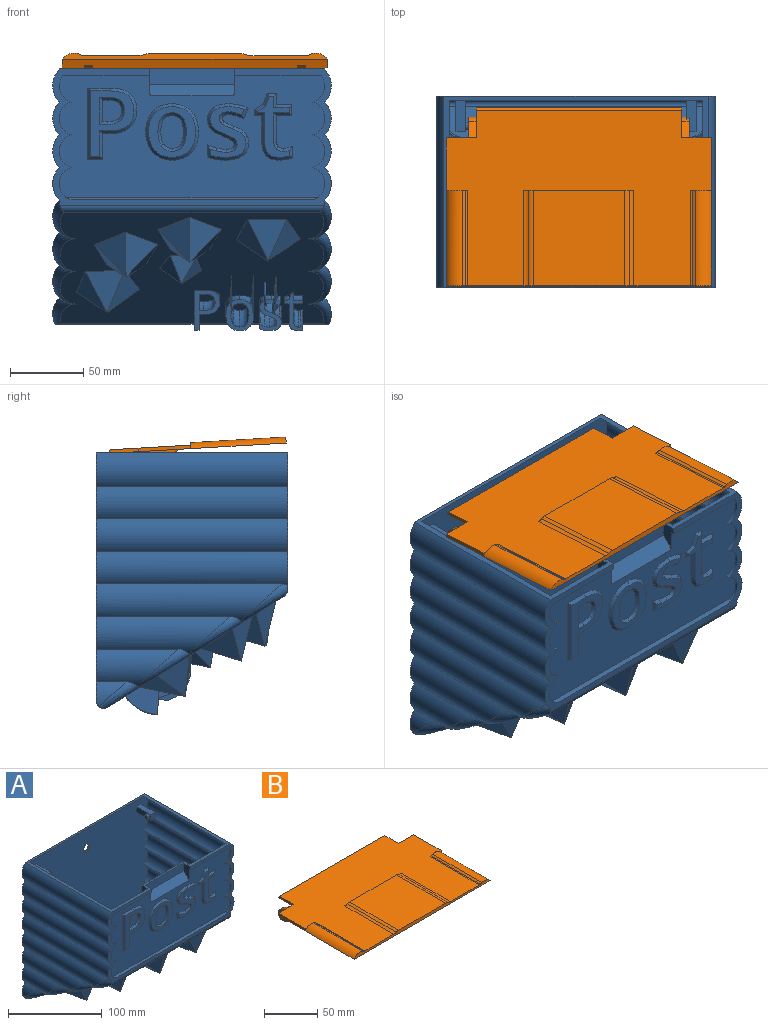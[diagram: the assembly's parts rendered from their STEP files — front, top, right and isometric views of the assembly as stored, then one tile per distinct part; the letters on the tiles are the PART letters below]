
ASSEMBLY  parts=2 mates=1
PART A: 296 faces, bbox 194.2x139.1x180.6 mm
  f0: cylinder r=13.63mm len=124mm, axis (0,1,0), area 3216.3mm2, adj f1,f8,f50,f294
  f1: cylinder r=13.63mm len=124mm, axis (0,1,0), area 3216.3mm2, adj f0,f2,f8,f294
  f2: cylinder r=13.63mm len=124mm, axis (0,1,0), area 3216.3mm2, adj f1,f3,f8,f294
  f3: cylinder r=13.63mm len=124mm, axis (0,1,0), area 3297.8mm2, adj f2,f8,f24,f294
  f4: cylinder r=13.63mm len=124mm, axis (0,1,0), area 3297.8mm2, adj f5,f8,f24,f294
  f5: cylinder r=13.63mm len=124mm, axis (0,1,0), area 3216.3mm2, adj f4,f6,f8,f294
  f6: cylinder r=13.63mm len=124mm, axis (0,1,0), area 3216.3mm2, adj f5,f7,f8,f294
  f7: cylinder r=13.63mm len=124mm, axis (0,1,0), area 3216.3mm2, adj f6,f8,f51,f294
  f8: plane 184.57x168.8mm, normal (0,-1,0), area 30406.4mm2, adj f0,f1,f2,f3,f4,f5,f6,f7
  f9: plane 182.54x84.64mm, normal (0,-1,0), area 10256.5mm2, adj f10,f11,f31,f32,f70,f71,f72,f73
  f10: cylinder r=5mm len=3mm, axis (0,-1,0), area 4.8mm2, adj f9,f31,f164
  f11: cylinder r=5mm len=3mm, axis (0,-1,0), area 4.8mm2, adj f9,f32,f164
  f12: plane 189.57x168.8mm, normal (0,1,0), area 31462.7mm2, adj f14,f15,f16,f17,f18,f19,f20,f21
  f13: plane 189.86x93.45mm, normal (0,-1,0), area 2168.8mm2, adj f20,f21,f22,f23,f24,f25,f26,f27
  f14: cylinder r=16.13mm len=55.43mm, axis (0,1,0), area 1109.7mm2, adj f12,f15,f30,f39,f41
  f15: cylinder r=16.13mm len=20.21mm, axis (0,1,0), area 195.6mm2, adj f12,f14,f41,f43
  f16: cylinder r=16.13mm len=20.21mm, axis (0,1,0), area 195.6mm2, adj f12,f17,f43,f44
  f17: cylinder r=16.13mm len=55.43mm, axis (0,1,0), area 1109.7mm2, adj f12,f16,f18,f42,f44
  f18: cylinder r=16.13mm len=90.65mm, axis (0,1,0), area 1971.9mm2, adj f12,f17,f19,f40,f42
  f19: cylinder r=16.13mm len=125.87mm, axis (0,1,0), area 2834.1mm2, adj f12,f18,f20,f38,f40
  f20: cylinder r=16.13mm len=130mm, axis (0,1,0), area 3184.8mm2, adj f12,f13,f19,f21,f38
  f21: cylinder r=16.13mm len=130mm, axis (0,1,0), area 3182.6mm2, adj f12,f13,f20,f22
  f22: cylinder r=16.13mm len=130mm, axis (0,1,0), area 3182.6mm2, adj f12,f13,f21,f23
  f23: cylinder r=16.13mm len=130mm, axis (0,1,0), area 3249.7mm2, adj f12,f13,f22,f24
  f24: plane 180x130mm, normal (0,0,1), area 2052.6mm2, adj f3,f4,f8,f12,f13,f23,f25,f31
  f25: cylinder r=16.13mm len=130mm, axis (0,1,0), area 3249.7mm2, adj f12,f13,f24,f26
  f26: cylinder r=16.13mm len=130mm, axis (0,1,0), area 3182.6mm2, adj f12,f13,f25,f27
  f27: cylinder r=16.13mm len=130mm, axis (0,1,0), area 3182.6mm2, adj f12,f13,f26,f28
  f28: cylinder r=16.13mm len=130mm, axis (0,1,0), area 3184.8mm2, adj f12,f13,f27,f29,f35
  f29: cylinder r=16.13mm len=125.87mm, axis (0,1,0), area 2834.1mm2, adj f12,f28,f30,f35,f37
  f30: cylinder r=16.13mm len=90.65mm, axis (0,1,0), area 1971.9mm2, adj f12,f14,f29,f37,f39
  f31: plane 15.29x10mm, normal (1,0,0), area 118.8mm2, adj f9,f10,f13,f24,f33,f72,f164
  f32: plane 15.29x10mm, normal (-1,0,0), area 118.8mm2, adj f9,f11,f13,f24,f33,f70,f164
  f33: plane 58.15x10.29mm, normal (0,-1,0), area 598.2mm2, adj f24,f31,f32,f164
  f34: plane 181.94x122.37mm, normal (0,-0.53,-0.85), area 18554mm2, adj f35,f36,f37,f38,f39,f40,f41,f42
  f35: bspline ~40.65x29.36mm, area 302mm2, adj f13,f28,f29,f34,f36,f37
  f36: cylinder r=5mm len=179.61mm, axis (-1,0,0), area 892.5mm2, adj f13,f34,f35,f38
  f37: bspline ~52.64x32.27mm, area 346mm2, adj f29,f30,f34,f35,f39
  f38: bspline ~40.65x29.36mm, area 302mm2, adj f13,f19,f20,f34,f36,f40
  f39: bspline ~52.64x32.27mm, area 346mm2, adj f14,f30,f34,f37,f41
  f40: bspline ~52.64x32.27mm, area 346mm2, adj f18,f19,f34,f38,f42
  f41: bspline ~42.45x25.53mm, area 255.1mm2, adj f14,f15,f34,f39,f43
  f42: bspline ~52.64x32.27mm, area 346mm2, adj f17,f18,f34,f40,f44
  f43: cylinder r=5mm len=189.34mm, axis (1,0,0), area 1977.5mm2, adj f12,f15,f16,f34,f41,f44
  f44: bspline ~42.45x25.53mm, area 255.1mm2, adj f16,f17,f34,f42,f43
  f45: cylinder r=13.63mm len=55.16mm, axis (0,1,0), area 1092.7mm2, adj f8,f46,f52,f64,f66
  f46: cylinder r=13.63mm len=19.94mm, axis (0,1,0), area 184.2mm2, adj f8,f45,f66,f68
  f47: cylinder r=13.63mm len=19.94mm, axis (0,1,0), area 184.2mm2, adj f8,f48,f68,f69
  f48: cylinder r=13.63mm len=55.16mm, axis (0,1,0), area 1092.7mm2, adj f8,f47,f49,f67,f69
  f49: cylinder r=13.63mm len=90.38mm, axis (0,1,0), area 2006.2mm2, adj f8,f48,f50,f65,f67
  f50: cylinder r=13.63mm len=125mm, axis (0,1,0), area 2891.2mm2, adj f0,f8,f49,f63,f65,f291,f294
  f51: cylinder r=13.63mm len=125mm, axis (0,1,0), area 2891.2mm2, adj f7,f8,f52,f60,f62,f293,f294
  f52: cylinder r=13.63mm len=90.38mm, axis (0,1,0), area 2006.2mm2, adj f8,f45,f51,f62,f64
  f53: plane 15.29x9mm, normal (-1,0,0), area 137.6mm2, adj f24,f54,f58,f294
  f54: cylinder r=7.5mm len=9mm, axis (0,-1,0), area 106mm2, adj f53,f55,f58,f294
  f55: plane 48.15x9mm, normal (0,0,-1), area 433.4mm2, adj f54,f56,f58,f294
  f56: cylinder r=7.5mm len=9mm, axis (0,-1,0), area 106mm2, adj f55,f57,f58,f294
  f57: plane 15.29x9mm, normal (1,0,0), area 137.6mm2, adj f24,f56,f58,f294
  f58: plane 63.15x22.79mm, normal (0,1,0), area 1414.9mm2, adj f24,f53,f54,f55,f56,f57
  f59: plane 179.57x120mm, normal (0,0.53,0.85), area 24859.7mm2, adj f60,f61,f62,f63,f64,f65,f66,f67
  f60: bspline ~36.4x24.81mm, area 142mm2, adj f51,f59,f61,f62,f293
  f61: cylinder r=2.5mm len=177.1mm, axis (-1,0,0), area 443.1mm2, adj f59,f60,f63,f292
  f62: bspline ~43.98x27.27mm, area 177.8mm2, adj f51,f52,f59,f60,f64
  f63: bspline ~36.4x24.81mm, area 142mm2, adj f50,f59,f61,f65,f291
  f64: bspline ~43.98x27.27mm, area 177.8mm2, adj f45,f52,f59,f62,f66
  f65: bspline ~43.98x27.27mm, area 177.8mm2, adj f49,f50,f59,f63,f67
  f66: bspline ~33.79x20.69mm, area 129.8mm2, adj f45,f46,f59,f64,f68
  f67: bspline ~43.98x27.27mm, area 177.8mm2, adj f48,f49,f59,f65,f69
  f68: cylinder r=2.5mm len=184.3mm, axis (1,0,0), area 972.4mm2, adj f8,f46,f47,f59,f66,f69
  f69: bspline ~33.79x20.69mm, area 129.8mm2, adj f47,f48,f59,f67,f68
  f70: plane 58.89x2mm, normal (0,0,-1), area 117.8mm2, adj f9,f13,f32,f71
  f71: cylinder r=11.63mm len=18.07mm, axis (0,-1,0), area 44.4mm2, adj f9,f13,f70,f79
  f72: plane 58.89x2mm, normal (0,0,-1), area 117.8mm2, adj f9,f13,f31,f73
  f73: cylinder r=11.63mm len=18.07mm, axis (0,-1,0), area 44.4mm2, adj f9,f13,f72,f74
  f74: cylinder r=11.63mm len=22.2mm, axis (0,-1,0), area 58.9mm2, adj f9,f13,f73,f75
  f75: cylinder r=11.63mm len=22.2mm, axis (0,-1,0), area 58.9mm2, adj f9,f13,f74,f76
  f76: cylinder r=11.63mm len=22.2mm, axis (0,-1,0), area 54.7mm2, adj f9,f13,f75,f295
  f77: cylinder r=11.63mm len=22.2mm, axis (0,-1,0), area 54.7mm2, adj f9,f13,f78,f295
  f78: cylinder r=11.63mm len=22.2mm, axis (0,-1,0), area 58.9mm2, adj f9,f13,f77,f79
  f79: cylinder r=11.63mm len=22.2mm, axis (0,-1,0), area 58.9mm2, adj f9,f13,f71,f78
  f80: plane 45.89x30.91mm, normal (0,-1,0), area 560mm2, adj f104,f105,f106,f107,f108,f109,f110,f111
  f81: plane 14.86x13.3mm, normal (0,-1,0), area 163.4mm2, adj f113,f114,f115,f116,f117,f118,f119
  f82: plane 35.57x33.08mm, normal (0,-1,0), area 479mm2, adj f86,f87,f88,f89,f90,f91,f92,f93
  f83: plane 22.89x16.03mm, normal (0,-1,0), area 284.3mm2, adj f96,f97,f98,f99,f100,f101,f102,f103
  f84: plane 35.86x25.56mm, normal (0,-1,0), area 354mm2, adj f138,f139,f140,f141,f142,f143,f144,f145
  f85: plane 42.68x22.79mm, normal (0,-1,0), area 326.1mm2, adj f120,f121,f122,f123,f124,f125,f126,f127
  f86: bspline ~13.32x6.41mm, area 39.2mm2, adj f9,f82,f87,f88
  f87: bspline ~9.41x4.07mm, area 26.3mm2, adj f9,f82,f86,f89
  f88: bspline ~14.11x6.19mm, area 41mm2, adj f9,f82,f86,f90
  f89: bspline ~7.56x7.25mm, area 24.6mm2, adj f9,f82,f87,f91
  f90: bspline ~10.2x3.98mm, area 28.5mm2, adj f9,f82,f88,f92
  f91: bspline ~10.17x3.97mm, area 28.4mm2, adj f9,f82,f89,f93
  f92: bspline ~7.6x7.25mm, area 24.7mm2, adj f9,f82,f90,f94
  f93: bspline ~14.15x6.23mm, area 41.1mm2, adj f9,f82,f91,f95
  f94: bspline ~9.41x4.09mm, area 26.3mm2, adj f9,f82,f92,f95
  f95: bspline ~13.28x6.47mm, area 39.1mm2, adj f9,f82,f93,f94
  f96: bspline ~9.34x3.79mm, area 25.8mm2, adj f82,f83,f97,f98
  f97: bspline ~7.55x4.75mm, area 22mm2, adj f82,f83,f96,f99
  f98: bspline ~9.4x3.77mm, area 26mm2, adj f82,f83,f96,f100
  f99: bspline ~7.5x4.74mm, area 21.8mm2, adj f82,f83,f97,f101
  f100: bspline ~7.51x4.8mm, area 22mm2, adj f82,f83,f98,f102
  f101: bspline ~9.36x3.79mm, area 25.9mm2, adj f82,f83,f99,f103
  f102: bspline ~7.56x4.82mm, area 22.1mm2, adj f82,f83,f100,f103
  f103: bspline ~9.4x3.81mm, area 26mm2, adj f82,f83,f101,f102
  f104: plane 10.27x2mm, normal (0,-0.71,-0.71), area 23.4mm2, adj f9,f80,f105,f106
  f105: plane 19.23x2mm, normal (0.71,-0.71,0), area 48.7mm2, adj f9,f80,f104,f107
  f106: plane 48.43x2mm, normal (-0.71,-0.71,0), area 131.3mm2, adj f9,f80,f104,f108
  f107: plane 6.4x2mm, normal (0,-0.71,-0.71), area 15.3mm2, adj f9,f80,f105,f109
  f108: plane 15.47x2mm, normal (0,-0.71,0.71), area 40.9mm2, adj f9,f80,f106,f110
  f109: bspline ~13.9x5.67mm, area 39.9mm2, adj f9,f80,f107,f111
  f110: bspline ~13.4x5.34mm, area 38.2mm2, adj f9,f80,f108,f112
  f111: bspline ~11.96x6.18mm, area 35.3mm2, adj f9,f80,f109,f112
  f112: bspline ~11.31x5.86mm, area 33.2mm2, adj f9,f80,f110,f111
  f113: bspline ~6.84x4mm, area 19mm2, adj f80,f81,f114,f115
  f114: bspline ~7.01x4.4mm, area 19.9mm2, adj f80,f81,f113,f116
  f115: bspline ~7.5x3.72mm, area 20.6mm2, adj f80,f81,f113,f117
  f116: bspline ~8.33x3.87mm, area 23mm2, adj f80,f81,f114,f118
  f117: plane 6.66x2mm, normal (0,-0.71,-0.71), area 16mm2, adj f80,f81,f115,f119
  f118: plane 5.38x2mm, normal (0,-0.71,0.71), area 12.4mm2, adj f80,f81,f116,f119
  f119: plane 18.37x2mm, normal (0.71,-0.71,0), area 46.3mm2, adj f80,f81,f117,f118
  f120: plane 7.2x4.51mm, normal (-0.37,-0.71,0.6), area 17.8mm2, adj f9,f85,f121,f122
  f121: plane 9.17x4.3mm, normal (-0.66,-0.71,0.25), area 22.6mm2, adj f9,f85,f120,f123
  f122: plane 4.27x2mm, normal (-0.71,-0.71,0), area 7.7mm2, adj f9,f85,f120,f124
  f123: plane 6.46x2mm, normal (0,-0.71,0.71), area 13.5mm2, adj f9,f85,f121,f125
  f124: plane 6.83x2mm, normal (0,-0.71,-0.71), area 13.7mm2, adj f9,f85,f122,f126
  f125: plane 9.89x2mm, normal (0.71,-0.71,0), area 22.3mm2, adj f9,f85,f123,f127
  f126: plane 19.85x2mm, normal (-0.71,-0.71,0), area 53.3mm2, adj f9,f85,f124,f128
  f127: plane 12.37x2mm, normal (0,-0.71,0.71), area 29.3mm2, adj f9,f85,f125,f129
  f128: bspline ~9.2x4.25mm, area 25.7mm2, adj f9,f85,f126,f130
  f129: plane 7.59x2mm, normal (0.71,-0.71,0), area 15.8mm2, adj f9,f85,f127,f131
  f130: bspline ~8.83x4.41mm, area 24.9mm2, adj f9,f85,f128,f132
  f131: plane 12.37x2mm, normal (0,-0.71,-0.71), area 29.3mm2, adj f9,f85,f129,f133
  f132: bspline ~9.28x3.52mm, area 23.8mm2, adj f9,f85,f130,f134
  f133: plane 19.85x2mm, normal (0.71,-0.71,0), area 53.3mm2, adj f9,f85,f131,f135
  f134: plane 7.65x2.14mm, normal (0.71,-0.71,0), area 15.6mm2, adj f9,f85,f132,f136
  f135: bspline ~4.7x3.24mm, area 12.4mm2, adj f9,f85,f133,f137
  f136: bspline ~6.94x3.16mm, area 15.5mm2, adj f9,f85,f134,f137
  f137: bspline ~4.5x3.04mm, area 11.7mm2, adj f9,f85,f135,f136
  f138: bspline ~4.33x4.13mm, area 11.6mm2, adj f9,f84,f139,f140
  f139: bspline ~4.84x2.72mm, area 12.8mm2, adj f9,f84,f138,f141
  f140: bspline ~7.05x4.91mm, area 19.4mm2, adj f9,f84,f138,f142
  f141: bspline ~7.64x4.98mm, area 22.5mm2, adj f9,f84,f139,f143
  f142: bspline ~5.7x4.04mm, area 15.1mm2, adj f9,f84,f140,f144
  f143: bspline ~10.85x4.33mm, area 30.4mm2, adj f9,f84,f141,f145
  f144: bspline ~3.95x3.46mm, area 9.5mm2, adj f9,f84,f142,f146
  f145: bspline ~13.02x4.73mm, area 34mm2, adj f9,f84,f143,f147
  f146: bspline ~3.34x2.74mm, area 8.2mm2, adj f9,f84,f144,f148
  f147: plane 7.43x4.27mm, normal (0.65,-0.71,-0.27), area 16.7mm2, adj f9,f84,f145,f149
  f148: bspline ~7.51x5.18mm, area 24.6mm2, adj f9,f84,f146,f150
  f149: bspline ~5.98x3.86mm, area 13.2mm2, adj f9,f84,f147,f151
  f150: bspline ~6.7x2.9mm, area 18.5mm2, adj f9,f84,f148,f152
  f151: bspline ~5.54x2.77mm, area 15.1mm2, adj f9,f84,f149,f153
  f152: bspline ~7.18x4.16mm, area 15.3mm2, adj f9,f84,f150,f154
  f153: bspline ~6.48x4.42mm, area 20.5mm2, adj f9,f84,f151,f155
  f154: plane 8.45x2.1mm, normal (-0.71,-0.71,0), area 17.4mm2, adj f9,f84,f152,f156
  f155: bspline ~4x3.47mm, area 10.9mm2, adj f9,f84,f153,f157
  f156: bspline ~5.95x3.55mm, area 13.3mm2, adj f9,f84,f154,f158
  f157: bspline ~7.81x4.96mm, area 20.4mm2, adj f9,f84,f155,f159
  f158: bspline ~6.89x2.52mm, area 19mm2, adj f9,f84,f156,f160
  f159: bspline ~7.42x5mm, area 19.5mm2, adj f9,f84,f157,f161
  f160: bspline ~11.85x4.58mm, area 33.3mm2, adj f9,f84,f158,f162
  f161: bspline ~4.38x4.19mm, area 11.8mm2, adj f9,f84,f159,f163
  f162: bspline ~8.69x5.16mm, area 25.5mm2, adj f9,f84,f160,f163
  f163: bspline ~4.73x2.76mm, area 12.5mm2, adj f9,f84,f161,f162
  f164: plane 58.32x8.17mm, normal (0,-0.71,0.71), area 655.2mm2, adj f9,f10,f11,f31,f32,f33
  f165: plane 4.05x2.5mm, normal (0.87,0,-0.49), area 11.6mm2, adj f8,f12,f166,f170
  f166: plane 4.05x2.5mm, normal (0.87,0,0.49), area 11.6mm2, adj f8,f12,f165,f167
  f167: cylinder r=3mm len=5.23mm, axis (0,-1,0), area 15.9mm2, adj f8,f12,f166,f168
  f168: plane 4.05x2.5mm, normal (-0.87,0,0.49), area 11.6mm2, adj f8,f12,f167,f169
  f169: plane 4.05x2.5mm, normal (-0.87,0,-0.49), area 11.6mm2, adj f8,f12,f168,f170
  f170: cylinder r=3mm len=5.23mm, axis (0,-1,0), area 15.9mm2, adj f8,f12,f165,f169
  f171: plane 7.63x6.7mm, normal (0,-1,0), area 51.2mm2, adj f172,f173,f174,f175
  f172: plane 21.7x6.7mm, normal (0,0,-1), area 145.4mm2, adj f8,f171,f174,f175
  f173: plane 21.7x6.7mm, normal (0,0,1), area 145.4mm2, adj f8,f171,f174,f175
  f174: plane 21.7x7.63mm, normal (-1,0,0), area 165.7mm2, adj f8,f171,f172,f173
  f175: plane 21.7x7.63mm, normal (1,0,0), area 141.1mm2, adj f8,f171,f172,f173,f176
  f176: cone r=2.8mm half-angle=10deg, axis (-1,0,0), area 48.5mm2, adj f175,f177
  f177: plane 4.54x4.54mm, normal (1,0,0), area 16.2mm2, adj f176
  f178: plane 7.63x6.7mm, normal (0,-1,0), area 51.2mm2, adj f179,f180,f181,f182
  f179: plane 21.7x6.7mm, normal (0,0,-1), area 145.4mm2, adj f8,f178,f181,f182
  f180: plane 21.7x6.7mm, normal (0,0,1), area 145.4mm2, adj f8,f178,f181,f182
  f181: plane 21.7x7.63mm, normal (1,0,0), area 165.7mm2, adj f8,f178,f179,f180
  f182: plane 21.7x7.63mm, normal (-1,0,0), area 141.1mm2, adj f8,f178,f179,f180,f183
  f183: cone r=2.8mm half-angle=10deg, axis (1,0,0), area 48.5mm2, adj f182,f184
  f184: plane 4.54x4.54mm, normal (-1,0,0), area 16.2mm2, adj f183
  f185: plane 30.63x21.68mm, normal (-0.46,-0.86,-0.22), area 381.5mm2, adj f34,f186,f189
  f186: plane 27.35x22.13mm, normal (-0.73,-0.14,-0.67), area 381.5mm2, adj f34,f185,f187
  f187: plane 27.35x26.69mm, normal (0.01,0.31,-0.95), area 381.5mm2, adj f34,f186,f188
  f188: plane 27.08x22.4mm, normal (0.73,-0.15,-0.67), area 381.5mm2, adj f34,f187,f189
  f189: plane 30.63x21.78mm, normal (0.44,-0.87,-0.21), area 381.5mm2, adj f34,f185,f188
  f190: plane 30.63x21.68mm, normal (-0.46,-0.86,-0.22), area 381.5mm2, adj f34,f191,f194
  f191: plane 27.35x22.13mm, normal (-0.73,-0.14,-0.67), area 381.5mm2, adj f34,f190,f192
  f192: plane 27.35x26.69mm, normal (0.01,0.31,-0.95), area 381.5mm2, adj f34,f191,f193
  f193: plane 27.08x22.4mm, normal (0.73,-0.15,-0.67), area 381.5mm2, adj f34,f192,f194
  f194: plane 30.63x21.78mm, normal (0.44,-0.87,-0.21), area 381.5mm2, adj f34,f190,f193
  f195: plane 27.7x21.97mm, normal (-0.75,-0.49,-0.45), area 381.5mm2, adj f34,f196,f199
  f196: plane 30.82x22.8mm, normal (-0.4,0.21,-0.89), area 381.5mm2, adj f34,f195,f197
  f197: plane 30.82x22.1mm, normal (0.5,0.15,-0.85), area 381.5mm2, adj f34,f196,f198
  f198: plane 28.86x22.1mm, normal (0.71,-0.59,-0.39), area 381.5mm2, adj f34,f197,f199
  f199: plane 28.86x26.61mm, normal (-0.06,-0.99,-0.14), area 381.5mm2, adj f34,f195,f198
  f200: plane 19.23x14.72mm, normal (-0.7,-0.61,-0.38), area 167.8mm2, adj f34,f201,f204
  f201: plane 20.42x14.72mm, normal (-0.51,0.14,-0.85), area 167.8mm2, adj f34,f200,f202
  f202: plane 20.42x15.31mm, normal (0.38,0.22,-0.9), area 167.8mm2, adj f34,f201,f203
  f203: plane 18.26x14.64mm, normal (0.75,-0.48,-0.46), area 167.8mm2, adj f34,f202,f204
  f204: plane 19.23x17.61mm, normal (0.08,-0.99,-0.14), area 167.8mm2, adj f34,f200,f203
  f205: plane 28.52x26.68mm, normal (-0.02,-0.99,-0.14), area 381.5mm2, adj f34,f206,f209
  f206: plane 28.1x21.67mm, normal (-0.74,-0.52,-0.43), area 381.5mm2, adj f34,f205,f207
  f207: plane 30.88x22.05mm, normal (-0.43,0.19,-0.88), area 381.5mm2, adj f34,f206,f208
  f208: plane 30.88x21.79mm, normal (0.47,0.17,-0.87), area 381.5mm2, adj f34,f207,f209
  f209: plane 28.52x21.79mm, normal (0.72,-0.56,-0.41), area 381.5mm2, adj f34,f205,f208
  f210: plane 12.14x11.56mm, normal (1,0,0), area 86.4mm2, adj f211,f223,f224,f225
  f211: cylinder r=3mm len=3.57mm, axis (1,0,0), area 8.5mm2, adj f210,f212,f224,f225
  f212: revolved ~5.56x3.23mm, area 16.1mm2, adj f211,f213,f224,f225
  f213: revolved ~6.61x5.86mm, area 25.1mm2, adj f212,f214,f224,f225
  f214: revolved ~10.14x8.03mm, area 48.9mm2, adj f213,f215,f224,f225
  f215: revolved ~11.09x6.95mm, area 81.2mm2, adj f214,f223,f224,f225
  f216: plane 27.06x23.13mm, normal (-1,0,0), area 354.6mm2, adj f34,f217,f224
  f217: cylinder r=27.69mm len=21.82mm, axis (1,0,0), area 83.3mm2, adj f34,f216,f218,f224
  f218: plane 22.34x18.24mm, normal (1,0,0), area 225.8mm2, adj f34,f217,f219,f224
  f219: cylinder r=16.89mm len=13.21mm, axis (1,0,0), area 50.8mm2, adj f34,f218,f220,f224
  f220: revolved ~13.31x8.71mm, area 129.6mm2, adj f34,f219,f221,f224
  f221: revolved ~11.73x10.01mm, area 77.7mm2, adj f34,f220,f222,f224
  f222: revolved ~7.88x6.66mm, area 24.3mm2, adj f34,f221,f224
  f223: cylinder r=14.15mm len=11.02mm, axis (1,0,0), area 37.7mm2, adj f210,f215,f224,f225
  f224: plane 27.43x17.41mm, normal (0,-1,-0.05), area 182.3mm2, adj f34,f210,f211,f212,f213,f214,f215,f216
  f225: plane 11.88x10.43mm, normal (0,-0.53,-0.85), area 108.5mm2, adj f210,f211,f212,f213,f214,f215,f223
  f226: revolved ~13.97x12.01mm, area 102.8mm2, adj f34,f227,f242,f243
  f227: revolved ~7.53x6.86mm, area 52.9mm2, adj f34,f226,f228,f243
  f228: revolved ~7.47x6.99mm, area 53.3mm2, adj f34,f227,f229,f243
  f229: revolved ~13.97x12.05mm, area 103.2mm2, adj f34,f228,f230,f243
  f230: revolved ~18.4x13.45mm, area 110.7mm2, adj f34,f229,f231,f243
  f231: revolved ~21.27x14.09mm, area 119mm2, adj f34,f230,f232,f243
  f232: revolved ~22.19x13.37mm, area 133.8mm2, adj f34,f231,f233,f243
  f233: revolved ~22.26x14.21mm, area 199.4mm2, adj f34,f232,f242,f243
  f234: revolved ~13.88x11.02mm, area 83.3mm2, adj f235,f241,f243,f244
  f235: revolved ~8.91x6.04mm, area 47.8mm2, adj f234,f236,f243,f244
  f236: revolved ~8.94x6.07mm, area 48.6mm2, adj f235,f237,f243,f244
  f237: revolved ~13.88x11mm, area 83.1mm2, adj f236,f238,f243,f244
  f238: revolved ~18.69x13.8mm, area 121.4mm2, adj f237,f239,f243,f244
  f239: revolved ~20.14x12.57mm, area 123.1mm2, adj f238,f240,f243,f244
  f240: revolved ~20.14x12.58mm, area 122.9mm2, adj f239,f241,f243,f244
  f241: revolved ~18.68x13.79mm, area 121.2mm2, adj f234,f240,f243,f244
  f242: revolved ~20.25x15.66mm, area 170mm2, adj f34,f226,f233,f243
  f243: plane 21.32x18.91mm, normal (0,-1,-0.05), area 162.7mm2, adj f226,f227,f228,f229,f230,f231,f232,f233
  f244: plane 14.34x13.18mm, normal (0,-0.53,-0.85), area 166.1mm2, adj f234,f235,f236,f237,f238,f239,f240,f241
  f245: revolved ~17.51x11.75mm, area 70.8mm2, adj f34,f246,f269,f270
  f246: revolved ~14.76x9.78mm, area 90.7mm2, adj f34,f245,f247,f270
  f247: revolved ~12.56x7.89mm, area 55.5mm2, adj f34,f246,f248,f270
  f248: revolved ~11.32x6.95mm, area 22.8mm2, adj f34,f247,f249,f270
  f249: revolved ~10.46x6.61mm, area 17.5mm2, adj f34,f248,f250,f270
  f250: revolved ~9.36x6.24mm, area 23.2mm2, adj f34,f249,f251,f270
  f251: revolved ~7.77x4.66mm, area 30mm2, adj f34,f250,f252,f270
  f252: revolved ~8.26x5.61mm, area 51.7mm2, adj f34,f251,f253,f270
  f253: cone r=8.08mm half-angle=66.3deg, axis (-1,0,0), area 23.5mm2, adj f34,f252,f254,f270
  f254: revolved ~6.5x6.24mm, area 42.9mm2, adj f34,f253,f255,f270
  f255: revolved ~6.33x5.61mm, area 37.8mm2, adj f34,f254,f256,f270
  f256: revolved ~9.62x7.51mm, area 42.5mm2, adj f34,f255,f257,f270
  f257: revolved ~11.48x7.74mm, area 31.2mm2, adj f34,f256,f258,f270
  f258: revolved ~12.9x8.23mm, area 37.2mm2, adj f34,f257,f259,f270
  f259: revolved ~14.39x9.13mm, area 72.9mm2, adj f34,f258,f260,f270
  f260: revolved ~16.01x10.15mm, area 81.7mm2, adj f34,f259,f261,f270
  f261: revolved ~17.65x11.12mm, area 47.5mm2, adj f34,f260,f262,f270
  f262: revolved ~19.56x12.4mm, area 63.4mm2, adj f34,f261,f263,f270
  f263: revolved ~20.1x11.89mm, area 92.1mm2, adj f34,f262,f264,f270
  f264: revolved ~20.09x11.69mm, area 79mm2, adj f34,f263,f265,f270
  f265: revolved ~19.78x11.91mm, area 78.4mm2, adj f34,f264,f266,f270
  f266: plane 21.23x13.6mm, normal (-1,0,0), area 68.9mm2, adj f34,f265,f267,f270
  f267: revolved ~22.19x13.37mm, area 171.7mm2, adj f34,f266,f268,f270
  f268: revolved ~22.2x13.51mm, area 164.1mm2, adj f34,f267,f269,f270
  f269: revolved ~21.09x14.36mm, area 117.9mm2, adj f34,f245,f268,f270
  f270: plane 21.32x14.59mm, normal (0,-1,-0.05), area 130mm2, adj f245,f246,f247,f248,f249,f250,f251,f252
  f271: revolved ~20.12x12mm, area 64mm2, adj f34,f272,f289,f290
  f272: revolved ~19.41x12.56mm, area 66.3mm2, adj f34,f271,f273,f290
  f273: plane 17.59x16.13mm, normal (1,0,0), area 175.4mm2, adj f34,f272,f274,f290
  f274: cylinder r=9.53mm len=7.33mm, axis (1,0,0), area 51.7mm2, adj f34,f273,f275,f290
  f275: plane 7.45x5.32mm, normal (1,0,0), area 18.2mm2, adj f34,f274,f276,f290
  f276: cylinder r=7.11mm len=5.97mm, axis (1,0,0), area 37.8mm2, adj f34,f275,f277,f290
  f277: plane 5.63x5.47mm, normal (1,0,0), area 19.3mm2, adj f34,f276,f278,f290
  f278: cylinder r=2.34mm len=1.8mm, axis (1,0,0), area 3.2mm2, adj f34,f277,f279,f290
  f279: cone r=6.73mm half-angle=73.4deg, axis (-1,0,0), area 17.2mm2, adj f34,f278,f280,f290
  f280: cone r=8.03mm half-angle=23.7deg, axis (-1,0,0), area 21.2mm2, adj f34,f279,f281,f290
  f281: plane 7.4x4.83mm, normal (-1,0,0), area 11.9mm2, adj f34,f280,f282,f290
  f282: cylinder r=9.53mm len=7.33mm, axis (1,0,0), area 25.6mm2, adj f34,f281,f283,f290
  f283: plane 17.7x16.26mm, normal (-1,0,0), area 178.1mm2, adj f34,f282,f284,f290
  f284: revolved ~22.43x16.11mm, area 242.1mm2, adj f34,f283,f285,f290
  f285: revolved ~22.13x12.75mm, area 47.2mm2, adj f34,f284,f286,f290
  f286: revolved ~22.01x12.8mm, area 40.5mm2, adj f34,f285,f287,f290
  f287: plane 21.79x13.67mm, normal (1,0,0), area 59.1mm2, adj f34,f286,f288,f290
  f288: revolved ~19.98x11.54mm, area 29.6mm2, adj f34,f287,f289,f290
  f289: revolved ~20.07x11.52mm, area 38.4mm2, adj f34,f271,f288,f290
  f290: plane 25.7x12.19mm, normal (0,-1,-0.05), area 109.6mm2, adj f271,f272,f273,f274,f275,f276,f277,f278
  f291: extruded ~3.53x1.49mm, area 4mm2, adj f50,f63,f292,f294
  f292: plane 177.1x1mm, normal (0,0,-1), area 177.1mm2, adj f61,f291,f293,f294
  f293: extruded ~3.53x1.49mm, area 4mm2, adj f51,f60,f292,f294
  f294: plane 184.59x93.18mm, normal (0,1,0), area 15437.9mm2, adj f0,f1,f2,f3,f4,f5,f6,f7
  f295: plane 172.15x2.35mm, normal (0,-0.71,0.71), area 476.9mm2, adj f9,f13,f76,f77
PART B: 41 faces, bbox 180.3x121.4x22.1 mm
  f0: plane 35.9x2.43mm, normal (1,0,0), area 87.1mm2, adj f2,f11,f20,f40
  f1: plane 35.9x2.43mm, normal (-1,0,0), area 87.1mm2, adj f2,f11,f19,f38
  f2: plane 180.32x121.4mm, normal (0,0,-1), area 20775.4mm2, adj f0,f1,f6,f14,f15,f21,f25,f26
  f3: plane 11.75x1.64mm, normal (0,1,0), area 12.1mm2, adj f11,f12,f13,f14
  f4: plane 74.92x1.32mm, normal (0,1,0), area 90.7mm2, adj f7,f8,f9,f10,f11,f18
  f5: plane 11.75x1.64mm, normal (0,1,0), area 12.1mm2, adj f11,f15,f16,f17
  f6: plane 180.32x4.07mm, normal (0,-1,0), area 546.7mm2, adj f2,f7,f8,f9,f10,f11,f12,f13
  f7: cylinder r=7.89mm len=65mm, axis (0,1,0), area 210.8mm2, adj f4,f6,f8,f18
  f8: plane 65x62.23mm, normal (0,0,1), area 4044.7mm2, adj f4,f6,f7,f9
  f9: cylinder r=7.89mm len=65mm, axis (0,1,0), area 210.8mm2, adj f4,f6,f8,f10
  f10: cylinder r=8mm len=65mm, axis (0,1,0), area 213.7mm2, adj f4,f6,f9,f11
  f11: plane 180.32x119.4mm, normal (0,0,1), area 14045.4mm2, adj f0,f1,f3,f4,f5,f6,f10,f12
  f12: cylinder r=5mm len=65mm, axis (0,1,0), area 79.5mm2, adj f3,f6,f11,f13
  f13: cylinder r=12.57mm len=65mm, axis (0,1,0), area 146.4mm2, adj f3,f6,f12,f14
  f14: cylinder r=10.05mm len=65mm, axis (0,1,0), area 809.9mm2, adj f2,f3,f6,f13,f20
  f15: cylinder r=10.05mm len=65mm, axis (0,1,0), area 809.9mm2, adj f2,f5,f6,f16,f19
  f16: cylinder r=12.57mm len=65mm, axis (0,1,0), area 146.4mm2, adj f5,f6,f15,f17
  f17: cylinder r=5mm len=65mm, axis (0,1,0), area 79.5mm2, adj f5,f6,f11,f16
  f18: cylinder r=8mm len=65mm, axis (0,1,0), area 213.7mm2, adj f4,f6,f7,f11
  f19: plane 2.57x2.43mm, normal (0,-1,0), area 2.7mm2, adj f1,f11,f15
  f20: plane 2.57x2.43mm, normal (0,-1,0), area 2.7mm2, adj f0,f11,f14
  f21: plane 34.41x17.41mm, normal (0,-0.45,-0.89), area 192.8mm2, adj f2,f22,f25,f26
  f22: cylinder r=6mm len=11.19mm, axis (-1,0,0), area 92.6mm2, adj f21,f23,f25,f26
  f23: plane 11.87x6.87mm, normal (0,0.5,0.87), area 68.6mm2, adj f22,f25,f26,f37
  f24: cylinder r=3mm len=6mm, axis (-1,0,0), area 94.2mm2, adj f25,f26
  f25: plane 43.12x18.06mm, normal (1,0,0), area 354.5mm2, adj f2,f21,f22,f23,f24,f37
  f26: plane 43.12x18.06mm, normal (-1,0,0), area 354.5mm2, adj f2,f21,f22,f23,f24,f37
  f27: plane 34.41x17.41mm, normal (0,-0.45,-0.89), area 192.8mm2, adj f2,f28,f31,f32
  f28: cylinder r=6mm len=11.19mm, axis (-1,0,0), area 92.6mm2, adj f27,f29,f31,f32
  f29: plane 11.87x6.87mm, normal (0,0.5,0.87), area 68.6mm2, adj f28,f31,f32,f39
  f30: cylinder r=3mm len=6mm, axis (-1,0,0), area 94.2mm2, adj f31,f32
  f31: plane 43.12x18.06mm, normal (1,0,0), area 354.5mm2, adj f2,f27,f28,f29,f30,f39
  f32: plane 43.12x18.06mm, normal (-1,0,0), area 354.5mm2, adj f2,f27,f28,f29,f30,f39
  f33: plane 20.5x2.43mm, normal (-1,0,0), area 47.7mm2, adj f2,f11,f35,f36,f38
  f34: plane 20.5x2.43mm, normal (1,0,0), area 47.7mm2, adj f2,f11,f35,f36,f40
  f35: plane 139.65x0.43mm, normal (0,1,0), area 59.4mm2, adj f2,f33,f34,f36
  f36: plane 139.65x2mm, normal (0,0.71,0.71), area 395mm2, adj f11,f33,f34,f35
  f37: plane 5x0.11mm, normal (0,0,1), area 0.5mm2, adj f23,f25,f26,f38
  f38: plane 20.44x2.43mm, normal (0,1,0), area 49.6mm2, adj f1,f2,f11,f33,f37
  f39: plane 5x0.11mm, normal (0,0,1), area 0.5mm2, adj f29,f31,f32,f40
  f40: plane 20.23x2.43mm, normal (0,1,0), area 49.1mm2, adj f0,f2,f11,f34,f39
PLACE A at identity fixed
PLACE B rot(axis=(-1,0,0),3.3deg) t=(2,-4.51,-1.04)mm
MATE revolute A.f176 <-> B.f22  axis (-1,0,0) through (72,-20.13,76.91)mm
